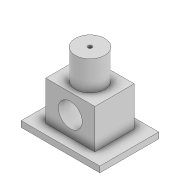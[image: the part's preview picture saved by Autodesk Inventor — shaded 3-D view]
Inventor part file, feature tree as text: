
AUTODESK INVENTOR PART (.ipt)
format: ipt  version: 2022 (Build 260153000, 153)  size: 128,512 bytes
history: native  units: mm
features: extrude x4, sketch x4, projected_geometry x1
ambient origin geometry x8: Origin, YZ Plane, XZ Plane, XY Plane, X Axis, Y Axis, Z Axis, Center Point
bodies: Solid1 (feature_tree)
feature tree (9):
  extrude  "Extrusion1"  Depth=25.0mm
  extrude  "Extrusion2"  Depth=20.0mm TaperAngle=0.0deg
  extrude  "Extrusion3"  Depth=100.0mm TaperAngle=0.0deg
  extrude  "Extrusion4"  Depth=15.0mm TaperAngle=0.0deg
  sketch  "Sketch1"  dims[d0=12.1mm d1=25.0mm]
  sketch  "Sketch2"  dims[d2=20.0mm d3=20.0mm d4=0.0mm]
  sketch  "Sketch3"  dims[d5=2.0mm d6=100.0mm d7=0.0mm]
  projected_geometry  "Projected Loop1"
  sketch  "Sketch4"  dims[d8=15.0mm d9=15.0mm d10=0.0mm d11=30.0mm d12=40.0mm d13=3.0mm d14=0.0mm]
